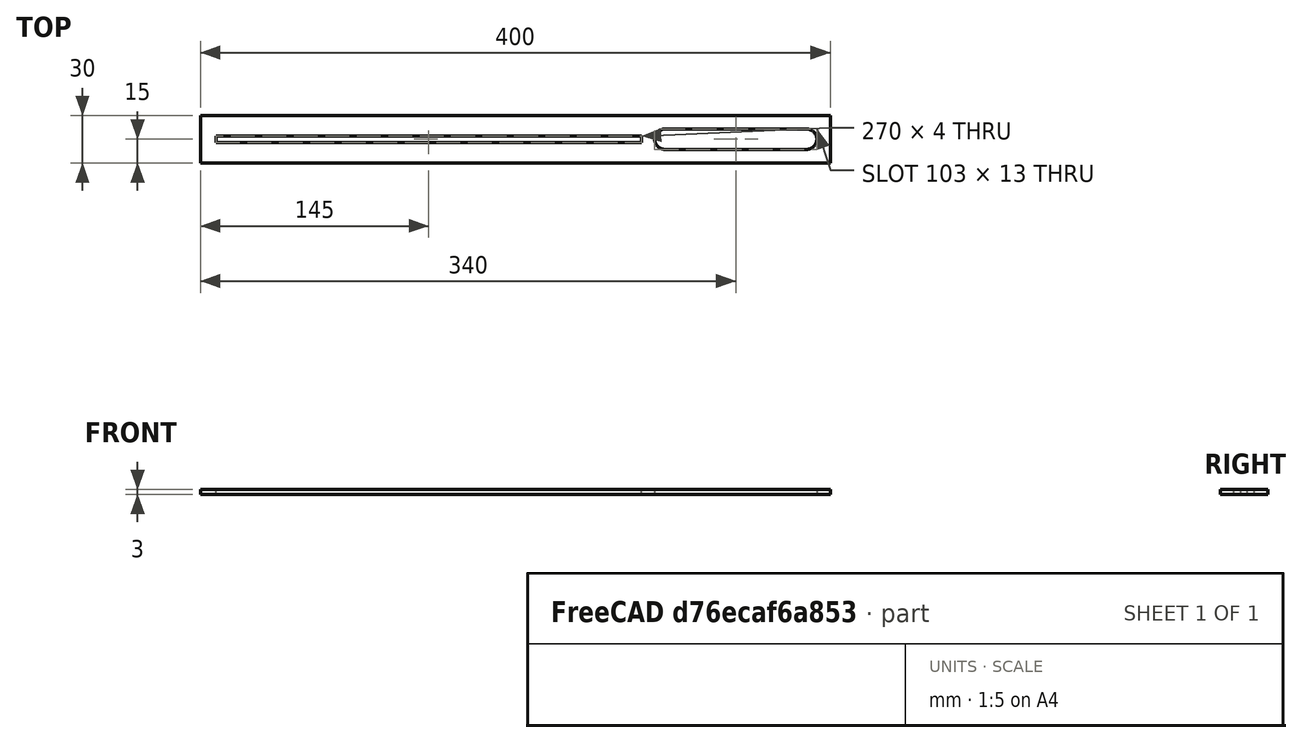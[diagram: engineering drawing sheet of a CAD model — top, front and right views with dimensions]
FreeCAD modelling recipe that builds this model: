
FCSTD DOCUMENT  (FreeCAD 0.18.4R)
Label: 接线盒固定座
License: All rights reserved
LicenseURL: http://en.wikipedia.org/wiki/All_rights_reserved
objects: TechDraw::DrawViewDimension×10, Sketcher::SketchObject×2, PartDesign::Pad×1, PartDesign::Pocket×1, PartDesign::Body×1, TechDraw::DrawSVGTemplate×1, TechDraw::DrawProjGroupItem×1, TechDraw::DrawProjGroup×1, TechDraw::DrawPage×1
note: 7 computed .brp shape members not serialized (recipe doc carries the construction recipe); baked Part::Feature solids carry a one-line shape summary decoded from their .brp

FEATURE [Sketcher::SketchObject] Sketch
  MapMode = 5
  Support = -> [XY_Plane]
  sketch-geometry (4):
    g0: LineSegment StartX=0 StartY=30 StartZ=0 EndX=400 EndY=30 EndZ=0
    g1: LineSegment StartX=400 StartY=30 StartZ=0 EndX=400 EndY=0 EndZ=0
    g2: LineSegment StartX=400 StartY=0 StartZ=0 EndX=0 EndY=0 EndZ=0
    g3: LineSegment StartX=0 StartY=0 StartZ=0 EndX=0 EndY=30 EndZ=0
  constraints (11):
    c: Coincident(g0,g1)
    c: Coincident(g1,g2)
    c: Coincident(g2,g3)
    c: Coincident(g3,g0)
    c: Horizontal(g0)
    c: Horizontal(g2)
    c: Vertical(g1)
    c: Vertical(g3)
    c: Coincident(g2,g-1)
    c: DistanceY(g1,g1) = 30
    c: DistanceX(g2,g2) = 400
FEATURE [PartDesign::Pad] Pad
  Length = 3
  Length2 = 100
  Profile = -> Sketch
  Type = 0
FEATURE [Sketcher::SketchObject] Sketch001
  ExternalGeometry = -> [Pad]
  MapMode = 5
  Support = -> [XY_Plane]
  sketch-geometry (9):
    g0: LineSegment StartX=10 StartY=13 StartZ=0 EndX=280 EndY=13 EndZ=0
    g1: LineSegment StartX=10 StartY=17 StartZ=0 EndX=280 EndY=17 EndZ=0
    g2: ArcOfCircle CenterX=295 CenterY=15 CenterZ=0 NormalX=0 NormalY=0 NormalZ=1 AngleXU=0 Radius=6.5 StartAngle=1.5708 EndAngle=4.71239
    g3: ArcOfCircle CenterX=385 CenterY=15 CenterZ=0 NormalX=0 NormalY=0 NormalZ=1 AngleXU=0 Radius=6.5 StartAngle=4.71239 EndAngle=7.85398
    g4: LineSegment StartX=295 StartY=8.5 StartZ=0 EndX=385 EndY=8.5 EndZ=0
    g5: LineSegment StartX=295 StartY=21.5 StartZ=0 EndX=385 EndY=21.5 EndZ=0
    g6: LineSegment [constr] StartX=385 StartY=15 StartZ=0 EndX=400 EndY=15 EndZ=0
    g7: LineSegment StartX=10 StartY=13 StartZ=0 EndX=10 EndY=17 EndZ=0
    g8: LineSegment StartX=280 StartY=17 StartZ=0 EndX=280 EndY=13 EndZ=0
  constraints (25):
    c: Horizontal(g0)
    c: Tangent(g2,g5) = 1.5708
    c: Tangent(g2,g4) = -1.5708
    c: Tangent(g4,g3) = -1.5708
    c: Tangent(g5,g3) = 1.5708
    c: Horizontal(g4)
    c: Equal(g2,g3)
    c: DistanceX(g4,g4) = 90
    c: Radius(g3) = 6.5
    c: DistanceY(g3) = 15
    c: PointOnObject(g6,g-3)
    c: Horizontal(g6)
    c: DistanceX(g6,g6) = 15
    c: Coincident(g3,g6)
    c: DistanceX(g0,g0) = 270
    c: Equal(g1,g0)
    c: DistanceX(g0) = 10
    c: DistanceY(g0) = 13
    c: Horizontal(g1)
    c: Coincident(g1,g8)
    c: Coincident(g0,g8)
    c: Coincident(g7,g1)
    c: Coincident(g7,g0)
    c: Vertical(g7)
    c: DistanceY(g7,g7) = 4
FEATURE [PartDesign::Pocket] Pocket
  BaseFeature = -> Pad
  Length = 0
  Length2 = 100
  Profile = -> Sketch001
  Reversed = true
  Type = 1
FEATURE [PartDesign::Body] Body
  Group = -> [Sketch,Pad,Sketch001,Pocket]
  Origin = -> Origin
  Tip = -> Pocket
FEATURE [TechDraw::DrawSVGTemplate] Template
  EditableTexts = Designed_by_Name=Yue Xiaokai; FC-Date=2020.11.23; FC-Title=接线盒固定架
  Height = 210
  Orientation = 1
  Width = 297
FEATURE [TechDraw::DrawProjGroupItem] ProjItem  label="Front"
  CoarseView = false
  Direction = (0,0,2)
  Focus = 100
  HardHidden = false
  IsoCount = 0
  IsoHidden = false
  IsoVisible = false
  LockPosition = true
  Perspective = false
  Rotation = 0
  RotationVector = (1,0,0)
  Scale = 0.5
  ScaleType = 2
  SeamHidden = false
  SeamVisible = false
  SmoothHidden = false
  SmoothVisible = false
  Source = -> [Pocket]
  Type = 0
  X = 0
  Y = 0
FEATURE [TechDraw::DrawProjGroup] ProjGroup
  Anchor = -> ProjItem
  AutoDistribute = true
  LockPosition = false
  ProjectionType = 0
  Rotation = 0
  Scale = 0.5
  ScaleType = 2
  Source = -> [Pocket]
  Views = -> [ProjItem]
  X = 130.017
  Y = 150.367
  spacingX = 15
  spacingY = 15
FEATURE [TechDraw::DrawViewDimension] Dimension
  Arbitrary = false
  FormatSpec = %f
  LockPosition = false
  MeasureType = 1
  OverTolerance = 0
  References2D = -> [ProjItem]
  Rotation = 0
  ScaleType = 0
  Type = 1
  UnderTolerance = 0
  X = -14.3418
  Y = -32.654
FEATURE [TechDraw::DrawViewDimension] Dimension001
  Arbitrary = false
  FormatSpec = %.2f
  LockPosition = false
  MeasureType = 1
  OverTolerance = 0
  References2D = -> [ProjItem]
  Rotation = 0
  ScaleType = 0
  Type = 2
  UnderTolerance = 0
  X = 120.373
  Y = 22.4821
FEATURE [TechDraw::DrawViewDimension] Dimension002
  Arbitrary = false
  FormatSpec = %.2f
  LockPosition = false
  MeasureType = 1
  OverTolerance = 0
  References2D = -> [ProjItem]
  Rotation = 0
  ScaleType = 0
  Type = 2
  UnderTolerance = 0
  X = -110.346
  Y = 14.4649
FEATURE [TechDraw::DrawViewDimension] Dimension003
  Arbitrary = false
  FormatSpec = %.2f
  LockPosition = false
  MeasureType = 1
  OverTolerance = 0
  References2D = -> [ProjItem]
  Rotation = 0
  ScaleType = 0
  Type = 1
  UnderTolerance = 0
  X = -79.302
  Y = 19.4905
FEATURE [TechDraw::DrawViewDimension] Dimension004
  Arbitrary = false
  FormatSpec = %f
  LockPosition = false
  MeasureType = 1
  OverTolerance = 0
  References2D = -> [ProjItem]
  Rotation = 0
  ScaleType = 0
  Type = 2
  UnderTolerance = 0
  X = -114.718
  Y = -23.4784
FEATURE [TechDraw::DrawViewDimension] Dimension005
  Arbitrary = false
  FormatSpec = %.2f
  LockPosition = false
  MeasureType = 1
  OverTolerance = 0
  References2D = -> [ProjItem]
  Rotation = 0
  ScaleType = 0
  Type = 1
  UnderTolerance = 0
  X = -36.2108
  Y = -18.5392
FEATURE [TechDraw::DrawViewDimension] Dimension006
  Arbitrary = false
  FormatSpec = %.2f
  LockPosition = false
  MeasureType = 1
  OverTolerance = 0
  References2D = -> [ProjItem]
  Rotation = 0
  ScaleType = 0
  Type = 1
  UnderTolerance = 0
  X = 73.3352
  Y = -12.6132
FEATURE [TechDraw::DrawViewDimension] Dimension007
  Arbitrary = false
  FormatSpec = R%.2f
  LockPosition = false
  MeasureType = 1
  OverTolerance = 0
  References2D = -> [ProjItem]
  Rotation = 0
  ScaleType = 0
  Type = 4
  UnderTolerance = 0
  X = 17.0087
  Y = 13.9273
FEATURE [TechDraw::DrawViewDimension] Dimension008
  Arbitrary = false
  FormatSpec = %.2f
  LockPosition = false
  MeasureType = 1
  OverTolerance = 0
  References2D = -> [ProjItem]
  Rotation = 0
  ScaleType = 0
  Type = 1
  UnderTolerance = 0
  X = 80.3946
  Y = 15.1969
FEATURE [TechDraw::DrawViewDimension] Dimension009
  Arbitrary = false
  FormatSpec = %.2f
  LockPosition = false
  MeasureType = 1
  OverTolerance = 0
  References2D = -> [ProjItem]
  Rotation = 0
  ScaleType = 0
  Type = 2
  UnderTolerance = 0
  X = 106.07
  Y = -20.2539
FEATURE [TechDraw::DrawPage] Page
  KeepUpdated = true
  ProjectionType = 0
  Template = -> Template
  Views = -> [ProjGroup,Dimension,Dimension001,Dimension002,Dimension003,Dimension004,Dimension005,Dimension006,Dimension007,Dimension008,Dimension009]
